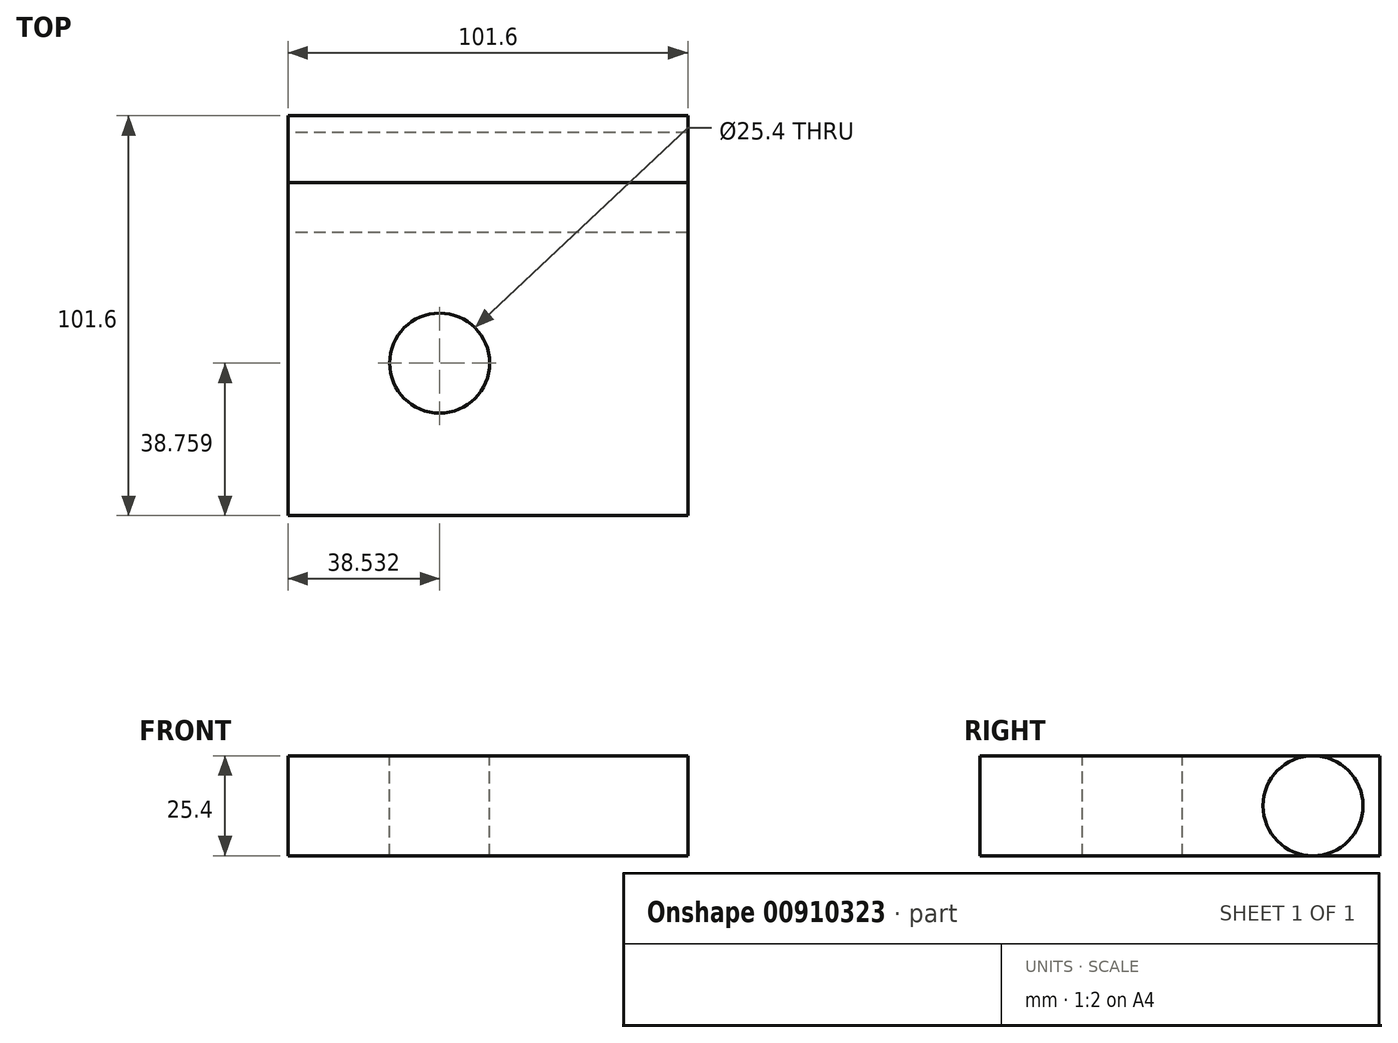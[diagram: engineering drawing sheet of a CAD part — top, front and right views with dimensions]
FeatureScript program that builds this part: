
annotation { "Feature Type Name" : "Feature", "Feature Type Description" : "" }
export const myFeature = defineFeature(function(context is Context, id is Id, definition is map)
    precondition{}
    {
        {
            var Q0;
            Q0=qCreatedBy(makeId("Top.planeOp"),FACE);
            var sketch = newSketch(context, id + "F0", { "sketchPlane" : qUnion([Q0])});
            skLineSegment(sketch, "E0.bottom", {"start": v(-141.42, -77) * mm, "end": v(-39.82, -77) * mm});
            skLineSegment(sketch, "E0.top", {"start": v(-141.42, 24.6) * mm, "end": v(-39.82, 24.6) * mm});
            skLineSegment(sketch, "E0.left", {"start": v(-141.42, -77) * mm, "end": v(-141.42, 24.6) * mm});
            skLineSegment(sketch, "E0.right", {"start": v(-39.82, -77) * mm, "end": v(-39.82, 24.6) * mm});
            skSolve(sketch);
        }
        {
            var Q0;
            Q0=makeQuery(id+"F0.imprint","IMPRINT",FACE,{"disambiguationData":[TD([[makeQuery(id+"F0.imprint","IMPRINT",EDGE,{"derivedFrom":sQuery(id+"F0.wireOp",EDGE,"E0.bottom")}),1.0]])]});
            extrude(context, id + "F1", {"entities" : qUnion([Q0]), "depth" : 25.4 * mm, "offsetDistance" : 25.4 * mm});
        }
        {
            var Q0;
            Q0=makeQuery(id+"F1.opExtrude","SWEPT_FACE",FACE,{"disambiguationData":[OSD([sQuery(id+"F0.wireOp",EDGE,"E0.left")])]});
            var sketch = newSketch(context, id + "F2", { "sketchPlane" : qUnion([Q0])});
            skCircle(sketch, "E1", {"center": v(-7.6, 12.7) * mm, "radius": 12.7 * mm});
            skPoint(sketch, "E1.centerSnap0", {"position": v(-24.6, 12.7) * mm});
            skSolve(sketch);
        }
        {
            var Q0;
            {var subQ0=sQuery(id+"F2.wireOp",EDGE,"E1");var subQ1=sQuery(id+"F0.wireOp",EDGE,"E0.left");var subQ2=makeQuery(id+"F2.imprint","INTERSECT",VERTEX,{"derivedFrom":[makeQuery(id+"F1.opExtrude","CAP_EDGE",EDGE,{"disambiguationData":[OSD([subQ1])],"isStart":true}),subQ0]});Q0=makeQuery(id+"F2.imprint","IMPRINT",FACE,{"disambiguationData":[TD([[makeQuery(id+"F2.imprint","IMPRINT",EDGE,{"disambiguationData":[TD([[subQ2,1.0]])],"derivedFrom":subQ0}),1.0]])]});}
            extrude(context, id + "F3", {"entities" : qUnion([Q0]), "operationType" : NewBodyOperationType.REMOVE, "endBound" : BoundingType.THROUGH_ALL, "oppositeDirection" : true, "depth" : 25.4 * mm, "offsetDistance" : 25.4 * mm});
        }
        {
            var Q0;
            {var subQ0=sQuery(id+"F0.wireOp",EDGE,"E0.bottom");var subQ1=sQuery(id+"F0.wireOp",EDGE,"E0.right");var subQ2=sQuery(id+"F0.wireOp",EDGE,"E0.left");Q0=makeQuery(id+"F3.boolean.opBoolean","SPLIT",FACE,{"disambiguationData":[TD([makeQuery(id+"F1.opExtrude","SWEPT_FACE",FACE,{"disambiguationData":[OSD([subQ0])]})])],"derivedFrom":makeQuery(id+"F1.opExtrude","CAP_FACE",FACE,{"disambiguationData":[OSD([subQ0,sQuery(id+"F0.wireOp",EDGE,"E0.top"),subQ2,subQ1])],"isStart":false})});}
            var sketch = newSketch(context, id + "F4", { "sketchPlane" : qUnion([Q0])});
            skCircle(sketch, "E2", {"center": v(-102.89, -38.24) * mm, "radius": 12.7 * mm});
            skSolve(sketch);
        }
        {
            var Q0;
            Q0=makeQuery(id+"F4.imprint","IMPRINT",FACE,{"disambiguationData":[TD([[makeQuery(id+"F4.imprint","IMPRINT",EDGE,{"derivedFrom":sQuery(id+"F4.wireOp",EDGE,"E2")}),1.0]])]});
            extrude(context, id + "F5", {"entities" : qUnion([Q0]), "operationType" : NewBodyOperationType.REMOVE, "endBound" : BoundingType.THROUGH_ALL, "oppositeDirection" : true, "depth" : 25.4 * mm, "offsetDistance" : 25.4 * mm});
        }
    });
